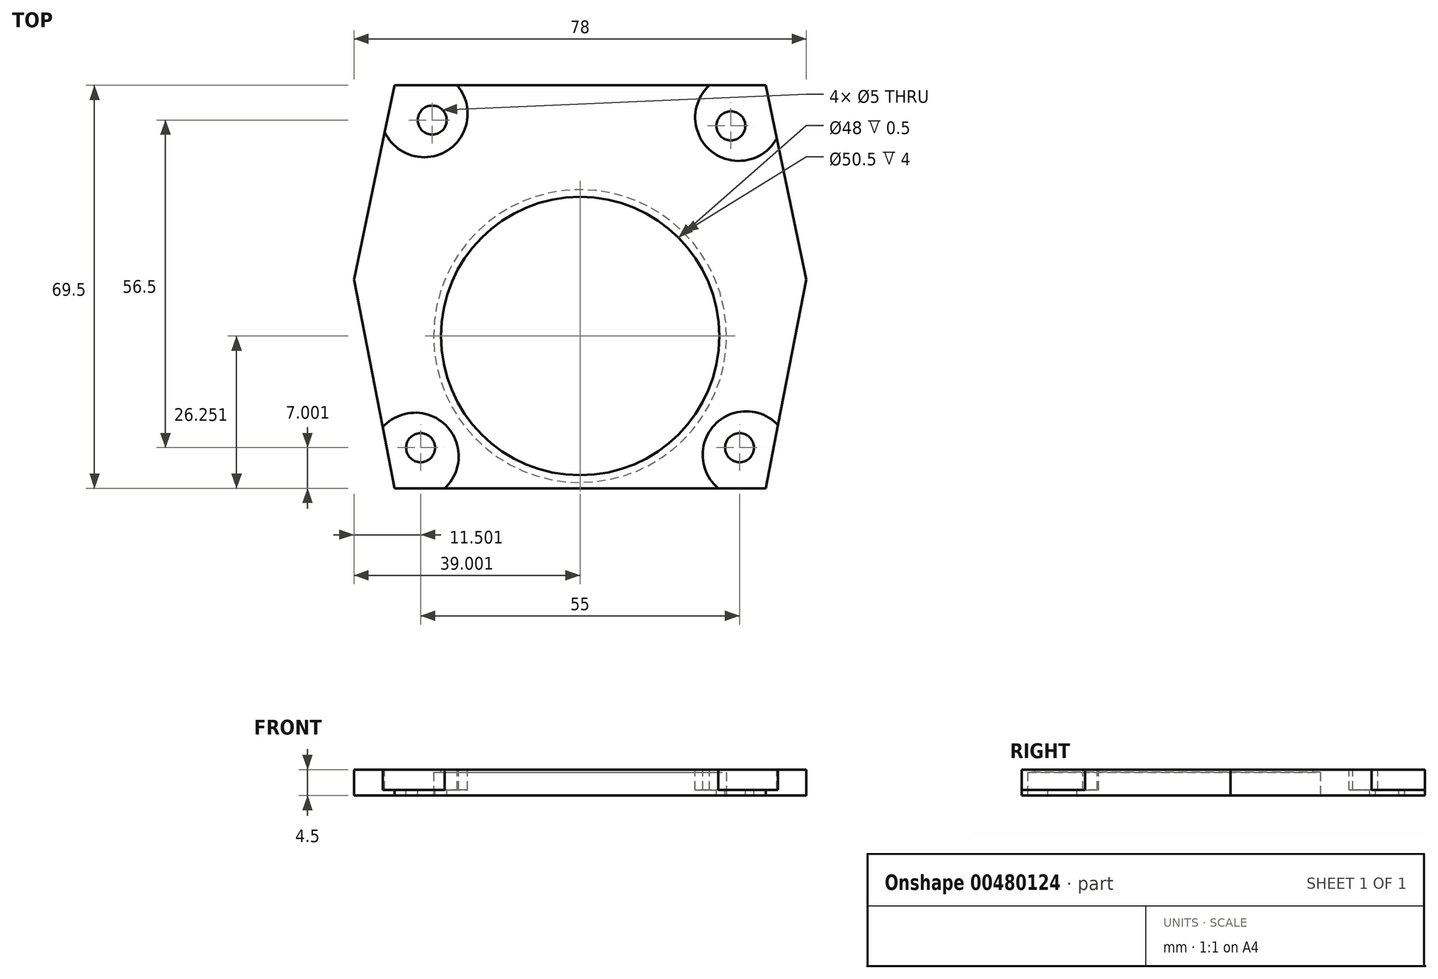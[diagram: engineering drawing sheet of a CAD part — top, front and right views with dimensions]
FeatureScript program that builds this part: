
annotation { "Feature Type Name" : "Feature", "Feature Type Description" : "" }
export const myFeature = defineFeature(function(context is Context, id is Id, definition is map)
    precondition{}
    {
        {
            var Q0;
            Q0=qCreatedBy(makeId("Top.planeOp"),FACE);
            var sketch = newSketch(context, id + "F0", { "sketchPlane" : qUnion([Q0])});
            skLineSegment(sketch, "E0.bottom", {"start": v(-110.02, -8.19) * mm, "end": v(-46.02, -8.19) * mm});
            skLineSegment(sketch, "E0.left", {"start": v(-110.02, -8.19) * mm, "end": v(-117.02, -41.69) * mm});
            skLineSegment(sketch, "E0.right", {"start": v(-46.02, -8.19) * mm, "end": v(-39.02, -41.69) * mm});
            skLineSegment(sketch, "E1", {"start": v(-117.02, -41.69) * mm, "end": v(-110.02, -77.69) * mm});
            skLineSegment(sketch, "E2", {"start": v(-110.02, -77.69) * mm, "end": v(-46.02, -77.69) * mm});
            skLineSegment(sketch, "E3", {"start": v(-46.02, -77.69) * mm, "end": v(-39.02, -41.69) * mm});
            skSolve(sketch);
        }
        {
            var Q0;
            Q0 = qSketchRegion(id + "F0", true);
            extrude(context, id + "F1", {"entities" : qUnion([Q0]), "depth" : 4.5 * mm});
        }
        {
            var Q0;
            Q0=makeQuery(id+"F1.opExtrude","CAP_FACE",FACE,{"disambiguationData":[OSD([sQuery(id+"F0.wireOp",EDGE,"E0.bottom"),sQuery(id+"F0.wireOp",EDGE,"E0.left"),sQuery(id+"F0.wireOp",EDGE,"E0.right"),sQuery(id+"F0.wireOp",EDGE,"E1"),sQuery(id+"F0.wireOp",EDGE,"E2"),sQuery(id+"F0.wireOp",EDGE,"E3")])],"isStart":false});
            var sketch = newSketch(context, id + "F2", { "sketchPlane" : qUnion([Q0])});
            skCircle(sketch, "E4", {"center": v(-103.52, -14.19) * mm, "radius": 2.5 * mm});
            skCircle(sketch, "E5", {"center": v(-52.02, -15.19) * mm, "radius": 2.5 * mm});
            skCircle(sketch, "E6", {"center": v(-105.52, -70.69) * mm, "radius": 2.5 * mm});
            skCircle(sketch, "E7", {"center": v(-50.52, -70.69) * mm, "radius": 2.5 * mm});
            skCircle(sketch, "E8", {"center": v(-78.02, -51.44) * mm, "radius": 24 * mm});
            skCircle(sketch, "E9", {"center": v(-78.02, -51.44) * mm, "radius": 25.25 * mm});
            skCircle(sketch, "E10", {"center": v(63.61, -2.78) * mm, "radius": 11 * mm});
            skCircle(sketch, "E11", {"center": v(36.71, -5.1) * mm, "radius": 11 * mm});
            skCircle(sketch, "E12", {"center": v(-106.45, -72.16) * mm, "radius": 7.5 * mm});
            skCircle(sketch, "E13", {"center": v(-50.67, -13.73) * mm, "radius": 7.5 * mm});
            skCircle(sketch, "E14", {"center": v(-104.92, -13.1) * mm, "radius": 7.5 * mm});
            skCircle(sketch, "E15", {"center": v(-49.39, -71.91) * mm, "radius": 7.5 * mm});
            skSolve(sketch);
        }
        {
            var Q0;
            Q0=makeQuery(id+"F2.imprint","IMPRINT",FACE,{"disambiguationData":[TD([[makeQuery(id+"F2.imprint","IMPRINT",EDGE,{"derivedFrom":sQuery(id+"F2.wireOp",EDGE,"E11")}),1.0]])]});
            var Q1;
            Q1=makeQuery(id+"F2.imprint","IMPRINT",FACE,{"disambiguationData":[TD([[makeQuery(id+"F2.imprint","IMPRINT",EDGE,{"derivedFrom":sQuery(id+"F2.wireOp",EDGE,"E10")}),1.0]])]});
            var Q2;
            Q2=makeQuery(id+"F2.imprint","IMPRINT",FACE,{"disambiguationData":[TD([[makeQuery(id+"F2.imprint","IMPRINT",EDGE,{"derivedFrom":sQuery(id+"F2.wireOp",EDGE,"afc35847-7ad4-4e10-bcfc-454a2d6fcaff")}),1.0]])]});
            var Q3;
            Q3=makeQuery(id+"F2.imprint","IMPRINT",FACE,{"disambiguationData":[TD([[makeQuery(id+"F2.imprint","IMPRINT",EDGE,{"derivedFrom":sQuery(id+"F2.wireOp",EDGE,"E8")}),1.0]])]});
            var Q4;
            Q4=makeQuery(id+"F2.imprint","IMPRINT",EDGE,{"derivedFrom":sQuery(id+"F2.wireOp",EDGE,"E11")});
            var Q5;
            Q5=sQuery(id+"F2.wireOp",EDGE,"E10");
            var Q6;
            Q6=sQuery(id+"F2.wireOp",EDGE,"afc35847-7ad4-4e10-bcfc-454a2d6fcaff");
            var Q7;
            Q7=sQuery(id+"F2.wireOp",EDGE,"E11");
            extrude(context, id + "F3", {"entities" : qUnion([Q0, Q1, Q2, Q3]), "operationType" : NewBodyOperationType.REMOVE, "surfaceEntities" : qUnion([Q4, Q5, Q6, Q7]), "oppositeDirection" : true, "depth" : 50 * mm});
        }
        {
            var Q0;
            Q0=makeQuery(id+"F2.imprint","IMPRINT",FACE,{"disambiguationData":[TD([[makeQuery(id+"F2.imprint","IMPRINT",EDGE,{"derivedFrom":sQuery(id+"F2.wireOp",EDGE,"E4")}),1.0]])]});
            var Q1;
            Q1=makeQuery(id+"F2.imprint","IMPRINT",FACE,{"disambiguationData":[TD([[makeQuery(id+"F2.imprint","IMPRINT",EDGE,{"derivedFrom":sQuery(id+"F2.wireOp",EDGE,"E5")}),1.0]])]});
            var Q2;
            Q2=makeQuery(id+"F2.imprint","IMPRINT",FACE,{"disambiguationData":[TD([[makeQuery(id+"F2.imprint","IMPRINT",EDGE,{"derivedFrom":sQuery(id+"F2.wireOp",EDGE,"E6")}),1.0]])]});
            var Q3;
            Q3=makeQuery(id+"F2.imprint","IMPRINT",FACE,{"disambiguationData":[TD([[makeQuery(id+"F2.imprint","IMPRINT",EDGE,{"derivedFrom":sQuery(id+"F2.wireOp",EDGE,"E7")}),1.0]])]});
            extrude(context, id + "F4", {"entities" : qUnion([Q0, Q1, Q2, Q3]), "operationType" : NewBodyOperationType.REMOVE, "oppositeDirection" : true, "depth" : 25 * mm});
        }
        {
            var Q0;
            Q0=makeQuery(id+"F2.imprint","IMPRINT",FACE,{"disambiguationData":[TD([[makeQuery(id+"F2.imprint","IMPRINT",EDGE,{"derivedFrom":sQuery(id+"F2.wireOp",EDGE,"E4")}),-1.0]])]});
            var Q1;
            Q1=makeQuery(id+"F2.imprint","IMPRINT",FACE,{"disambiguationData":[TD([[makeQuery(id+"F2.imprint","IMPRINT",EDGE,{"derivedFrom":sQuery(id+"F2.wireOp",EDGE,"E5")}),-1.0]])]});
            var Q2;
            Q2=makeQuery(id+"F2.imprint","IMPRINT",FACE,{"disambiguationData":[TD([[makeQuery(id+"F2.imprint","IMPRINT",EDGE,{"derivedFrom":sQuery(id+"F2.wireOp",EDGE,"E6")}),-1.0]])]});
            var Q3;
            Q3=makeQuery(id+"F2.imprint","IMPRINT",FACE,{"disambiguationData":[TD([[makeQuery(id+"F2.imprint","IMPRINT",EDGE,{"derivedFrom":sQuery(id+"F2.wireOp",EDGE,"E7")}),-1.0]])]});
            var Q4;
            Q4=sQuery(id+"F2.wireOp",EDGE,"E14");
            var Q5;
            Q5=sQuery(id+"F2.wireOp",EDGE,"E13");
            var Q6;
            Q6=sQuery(id+"F2.wireOp",EDGE,"E12");
            var Q7;
            Q7=sQuery(id+"F2.wireOp",EDGE,"E15");
            var Q8;
            Q8=sQuery(id+"F2.wireOp",EDGE,"E9");
            extrude(context, id + "F5", {"entities" : qUnion([Q0, Q1, Q2, Q3]), "operationType" : NewBodyOperationType.REMOVE, "surfaceEntities" : qUnion([Q4, Q5, Q6, Q7, Q8]), "oppositeDirection" : true, "depth" : 3.5 * mm});
        }
        {
            var Q0;
            Q0=makeQuery(id+"F2.imprint","IMPRINT",FACE,{"disambiguationData":[TD([[makeQuery(id+"F2.imprint","IMPRINT",EDGE,{"derivedFrom":sQuery(id+"F2.wireOp",EDGE,"E8")}),1.0]])]});
            extrude(context, id + "F6", {"entities" : qUnion([Q0]), "operationType" : NewBodyOperationType.REMOVE, "oppositeDirection" : true, "depth" : 2 * mm});
        }
        {
            var Q0;
            Q0=makeQuery(id+"F1.opExtrude","CAP_FACE",FACE,{"disambiguationData":[OSD([sQuery(id+"F0.wireOp",EDGE,"E0.bottom"),sQuery(id+"F0.wireOp",EDGE,"E0.left"),sQuery(id+"F0.wireOp",EDGE,"E0.right"),sQuery(id+"F0.wireOp",EDGE,"E1"),sQuery(id+"F0.wireOp",EDGE,"E2"),sQuery(id+"F0.wireOp",EDGE,"E3")])],"isStart":true});
            var sketch = newSketch(context, id + "F7", { "sketchPlane" : qUnion([Q0])});
            skCircle(sketch, "E16", {"center": v(-78.02, 51.44) * mm, "radius": 25.25 * mm});
            skSolve(sketch);
        }
        {
            var Q0;
            Q0 = qSketchRegion(id + "F7", true);
            extrude(context, id + "F8", {"entities" : qUnion([Q0]), "operationType" : NewBodyOperationType.REMOVE, "oppositeDirection" : true, "depth" : 4 * mm});
        }
    });
